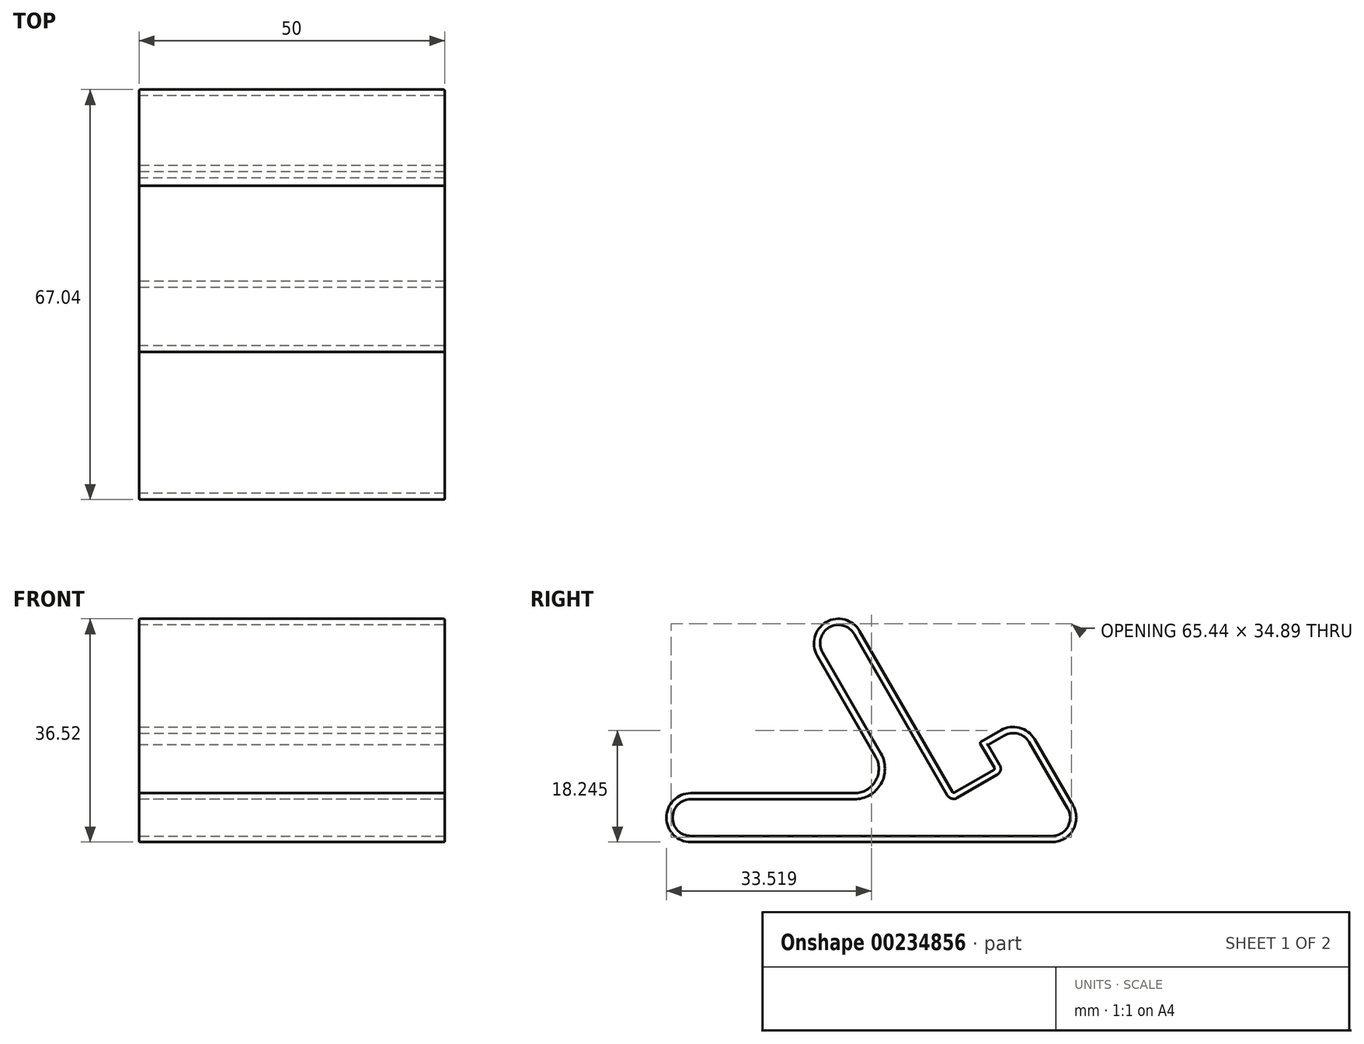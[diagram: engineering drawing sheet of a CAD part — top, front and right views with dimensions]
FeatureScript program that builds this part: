
annotation { "Feature Type Name" : "Feature", "Feature Type Description" : "" }
export const myFeature = defineFeature(function(context is Context, id is Id, definition is map)
    precondition{}
    {
        {
            var Q0;
            Q0=qCreatedBy(makeId("Right.planeOp"),FACE);
            var sketch = newSketch(context, id + "F0", { "sketchPlane" : qUnion([Q0])});
            skLineSegment(sketch, "E0", {"start": v(0, 0) * mm, "end": v(-11.82, 20.28) * mm});
            skLineSegment(sketch, "E1", {"start": v(-18.75, 16.28) * mm, "end": v(-16.25, 11.95) * mm});
            skLineSegment(sketch, "E2", {"start": v(-16.25, 11.95) * mm, "end": v(-23.1, 8) * mm});
            skLineSegment(sketch, "E3", {"start": v(-23.1, 8) * mm, "end": v(-40.4, 37.98) * mm});
            skLineSegment(sketch, "E4", {"start": v(-40.4, 37.98) * mm, "end": v(-47.33, 33.98) * mm});
            skLineSegment(sketch, "E5", {"start": v(-47.33, 33.98) * mm, "end": v(-32.33, 8) * mm});
            skLineSegment(sketch, "E6", {"start": v(-32.33, 8) * mm, "end": v(-70, 8) * mm});
            skLineSegment(sketch, "E7", {"start": v(-70, 8) * mm, "end": v(-70, 0) * mm});
            skLineSegment(sketch, "E8", {"start": v(-70, 0) * mm, "end": v(0, 0) * mm});
            skLineSegment(sketch, "E9", {"start": v(-18.75, 16.28) * mm, "end": v(-11.82, 20.28) * mm});
            skSolve(sketch);
        }
        {
            var Q0;
            Q0=makeQuery(id+"F0.imprint","IMPRINT",FACE,{"disambiguationData":[TD([[makeQuery(id+"F0.imprint","IMPRINT",EDGE,{"derivedFrom":sQuery(id+"F0.wireOp",EDGE,"E0")}),1.0]])]});
            extrude(context, id + "F1", {"entities" : qUnion([Q0]), "depth" : 50 * mm});
        }
        {
            var Q0;
            Q0=makeQuery(id+"F1.opExtrude","SWEPT_EDGE",EDGE,{"disambiguationData":[OSD([sQuery(id+"F0.wireOp",EDGE,"E0"),sQuery(id+"F0.wireOp",EDGE,"E8")])]});
            var Q1;
            Q1=makeQuery(id+"F1.opExtrude","SWEPT_EDGE",EDGE,{"disambiguationData":[OSD([sQuery(id+"F0.wireOp",EDGE,"E0"),sQuery(id+"F0.wireOp",EDGE,"E9")])]});
            var Q2;
            Q2=makeQuery(id+"F1.opExtrude","SWEPT_EDGE",EDGE,{"disambiguationData":[OSD([sQuery(id+"F0.wireOp",EDGE,"E3"),sQuery(id+"F0.wireOp",EDGE,"E4")])]});
            var Q3;
            Q3=makeQuery(id+"F1.opExtrude","SWEPT_EDGE",EDGE,{"disambiguationData":[OSD([sQuery(id+"F0.wireOp",EDGE,"E4"),sQuery(id+"F0.wireOp",EDGE,"E5")])]});
            var Q4;
            Q4=makeQuery(id+"F1.opExtrude","SWEPT_EDGE",EDGE,{"disambiguationData":[OSD([sQuery(id+"F0.wireOp",EDGE,"E5"),sQuery(id+"F0.wireOp",EDGE,"E6")])]});
            var Q5;
            Q5=makeQuery(id+"F1.opExtrude","SWEPT_EDGE",EDGE,{"disambiguationData":[OSD([sQuery(id+"F0.wireOp",EDGE,"E6"),sQuery(id+"F0.wireOp",EDGE,"E7")])]});
            var Q6;
            Q6=makeQuery(id+"F1.opExtrude","SWEPT_EDGE",EDGE,{"disambiguationData":[OSD([sQuery(id+"F0.wireOp",EDGE,"E7"),sQuery(id+"F0.wireOp",EDGE,"E8")])]});
            fillet(context, id + "F2", {"entities" : qUnion([Q0, Q1, Q2, Q3, Q4, Q5, Q6]), "radius" : 4 * mm, "tangentPropagation" : true, "allowEdgeOverflow" : false});
        }
        {
            var Q0;
            Q0=makeQuery(id+"F1.opExtrude","SWEPT_EDGE",EDGE,{"disambiguationData":[OSD([sQuery(id+"F0.wireOp",EDGE,"E1"),sQuery(id+"F0.wireOp",EDGE,"E9")])]});
            var Q1;
            Q1=makeQuery(id+"F1.opExtrude","SWEPT_EDGE",EDGE,{"disambiguationData":[OSD([sQuery(id+"F0.wireOp",EDGE,"E2"),sQuery(id+"F0.wireOp",EDGE,"E3")])]});
            var Q2;
            Q2=makeQuery(id+"F1.opExtrude","SWEPT_EDGE",EDGE,{"disambiguationData":[OSD([sQuery(id+"F0.wireOp",EDGE,"E1"),sQuery(id+"F0.wireOp",EDGE,"E2")])]});
            fillet(context, id + "F3", {"entities" : qUnion([Q0, Q1, Q2]), "radius" : 0.2 * mm, "tangentPropagation" : true, "allowEdgeOverflow" : false});
        }
        {
            var Q0;
            Q0=makeQuery(id+"F1.opExtrude","CAP_FACE",FACE,{"disambiguationData":[OSD([sQuery(id+"F0.wireOp",EDGE,"E0"),sQuery(id+"F0.wireOp",EDGE,"E1"),sQuery(id+"F0.wireOp",EDGE,"E2"),sQuery(id+"F0.wireOp",EDGE,"E3"),sQuery(id+"F0.wireOp",EDGE,"E4"),sQuery(id+"F0.wireOp",EDGE,"E5"),sQuery(id+"F0.wireOp",EDGE,"E6"),sQuery(id+"F0.wireOp",EDGE,"E7"),sQuery(id+"F0.wireOp",EDGE,"E8"),sQuery(id+"F0.wireOp",EDGE,"E9")])],"isStart":false});
            var Q1;
            Q1=makeQuery(id+"F1.opExtrude","CAP_FACE",FACE,{"disambiguationData":[OSD([sQuery(id+"F0.wireOp",EDGE,"E0"),sQuery(id+"F0.wireOp",EDGE,"E1"),sQuery(id+"F0.wireOp",EDGE,"E2"),sQuery(id+"F0.wireOp",EDGE,"E3"),sQuery(id+"F0.wireOp",EDGE,"E4"),sQuery(id+"F0.wireOp",EDGE,"E5"),sQuery(id+"F0.wireOp",EDGE,"E6"),sQuery(id+"F0.wireOp",EDGE,"E7"),sQuery(id+"F0.wireOp",EDGE,"E8"),sQuery(id+"F0.wireOp",EDGE,"E9")])],"isStart":true});
            fillet(context, id + "F4", {"entities" : qUnion([Q0, Q1]), "radius" : 0.2 * mm, "tangentPropagation" : true, "allowEdgeOverflow" : false});
        }
        {
            var Q0;
            Q0=makeQuery(id+"F1.opExtrude","CAP_FACE",FACE,{"disambiguationData":[OSD([sQuery(id+"F0.wireOp",EDGE,"E0"),sQuery(id+"F0.wireOp",EDGE,"E1"),sQuery(id+"F0.wireOp",EDGE,"E2"),sQuery(id+"F0.wireOp",EDGE,"E3"),sQuery(id+"F0.wireOp",EDGE,"E4"),sQuery(id+"F0.wireOp",EDGE,"E5"),sQuery(id+"F0.wireOp",EDGE,"E6"),sQuery(id+"F0.wireOp",EDGE,"E7"),sQuery(id+"F0.wireOp",EDGE,"E8"),sQuery(id+"F0.wireOp",EDGE,"E9")])],"isStart":false});
            var Q1;
            Q1=makeQuery(id+"F1.opExtrude","CAP_FACE",FACE,{"disambiguationData":[OSD([sQuery(id+"F0.wireOp",EDGE,"E0"),sQuery(id+"F0.wireOp",EDGE,"E1"),sQuery(id+"F0.wireOp",EDGE,"E2"),sQuery(id+"F0.wireOp",EDGE,"E3"),sQuery(id+"F0.wireOp",EDGE,"E4"),sQuery(id+"F0.wireOp",EDGE,"E5"),sQuery(id+"F0.wireOp",EDGE,"E6"),sQuery(id+"F0.wireOp",EDGE,"E7"),sQuery(id+"F0.wireOp",EDGE,"E8"),sQuery(id+"F0.wireOp",EDGE,"E9")])],"isStart":true});
            var Q2;
            Q2=makeQuery(id+"F1.opExtrude","SWEPT_BODY",BODY,{"disambiguationData":[OSD([sQuery(id+"F0.wireOp",EDGE,"E0"),sQuery(id+"F0.wireOp",EDGE,"E1"),sQuery(id+"F0.wireOp",EDGE,"E2"),sQuery(id+"F0.wireOp",EDGE,"E3"),sQuery(id+"F0.wireOp",EDGE,"E4"),sQuery(id+"F0.wireOp",EDGE,"E5"),sQuery(id+"F0.wireOp",EDGE,"E6"),sQuery(id+"F0.wireOp",EDGE,"E7"),sQuery(id+"F0.wireOp",EDGE,"E8"),sQuery(id+"F0.wireOp",EDGE,"E9")])]});
            shell(context, id + "F5", {"entities" : qUnion([Q0, Q1]), "parts" : qUnion([Q2]), "thickness" : 1 * mm});
        }
        {
            var Q0;
            Q0=makeQuery(id+"F1.opExtrude","CAP_FACE",FACE,{"disambiguationData":[OSD([sQuery(id+"F0.wireOp",EDGE,"E0"),sQuery(id+"F0.wireOp",EDGE,"E1"),sQuery(id+"F0.wireOp",EDGE,"E2"),sQuery(id+"F0.wireOp",EDGE,"E3"),sQuery(id+"F0.wireOp",EDGE,"E4"),sQuery(id+"F0.wireOp",EDGE,"E5"),sQuery(id+"F0.wireOp",EDGE,"E6"),sQuery(id+"F0.wireOp",EDGE,"E7"),sQuery(id+"F0.wireOp",EDGE,"E8"),sQuery(id+"F0.wireOp",EDGE,"E9")])],"isStart":false});
            var Q1;
            {var subQ0=sQuery(id+"F0.wireOp",EDGE,"E9");var subQ1=sQuery(id+"F0.wireOp",EDGE,"E8");var subQ2=sQuery(id+"F0.wireOp",EDGE,"E7");var subQ3=sQuery(id+"F0.wireOp",EDGE,"E6");var subQ4=sQuery(id+"F0.wireOp",EDGE,"E5");var subQ5=sQuery(id+"F0.wireOp",EDGE,"E4");var subQ6=sQuery(id+"F0.wireOp",EDGE,"E3");var subQ7=sQuery(id+"F0.wireOp",EDGE,"E2");var subQ8=sQuery(id+"F0.wireOp",EDGE,"E1");var subQ9=sQuery(id+"F0.wireOp",EDGE,"E0");var subQ10=makeQuery(id+"F1.opExtrude","CAP_EDGE",EDGE,{"disambiguationData":[OSD([subQ9])],"isStart":true});Q1=makeQuery(id+"F5.opShell","OFFSET_EDGE",EDGE,{"disambiguationData":[OSD([subQ9,subQ8,subQ7,subQ6,subQ5,subQ4,subQ3,subQ2,subQ1,subQ0]),TDD([makeQuery(id+"F4.opFillet","BLEND_EDGE",EDGE,{"blendedFrom":[subQ10,makeQuery(id+"F1.opExtrude","SWEPT_FACE",FACE,{"disambiguationData":[OSD([subQ9])]})],"blendedInto":[makeQuery(id+"F1.opExtrude","SWEPT_FACE",FACE,{"disambiguationData":[OSD([subQ9])]})]}),makeQuery(id+"F4.opFillet","BLEND_EDGE",EDGE,{"blendedFrom":[subQ10,makeQuery(id+"F1.opExtrude","CAP_FACE",FACE,{"disambiguationData":[OSD([subQ9,subQ8,subQ7,subQ6,subQ5,subQ4,subQ3,subQ2,subQ1,subQ0])],"isStart":true})],"blendedInto":[makeQuery(id+"F1.opExtrude","CAP_FACE",FACE,{"disambiguationData":[OSD([subQ9,subQ8,subQ7,subQ6,subQ5,subQ4,subQ3,subQ2,subQ1,subQ0])],"isStart":true})]})])]});}
            var Q2;
            Q2=makeQuery(id+"F1.opExtrude","CAP_FACE",FACE,{"disambiguationData":[OSD([sQuery(id+"F0.wireOp",EDGE,"E0"),sQuery(id+"F0.wireOp",EDGE,"E1"),sQuery(id+"F0.wireOp",EDGE,"E2"),sQuery(id+"F0.wireOp",EDGE,"E3"),sQuery(id+"F0.wireOp",EDGE,"E4"),sQuery(id+"F0.wireOp",EDGE,"E5"),sQuery(id+"F0.wireOp",EDGE,"E6"),sQuery(id+"F0.wireOp",EDGE,"E7"),sQuery(id+"F0.wireOp",EDGE,"E8"),sQuery(id+"F0.wireOp",EDGE,"E9")])],"isStart":true});
            fillet(context, id + "F6", {"entities" : qUnion([Q0, Q1, Q2]), "radius" : 0.2 * mm, "tangentPropagation" : true, "allowEdgeOverflow" : false});
        }
    });
